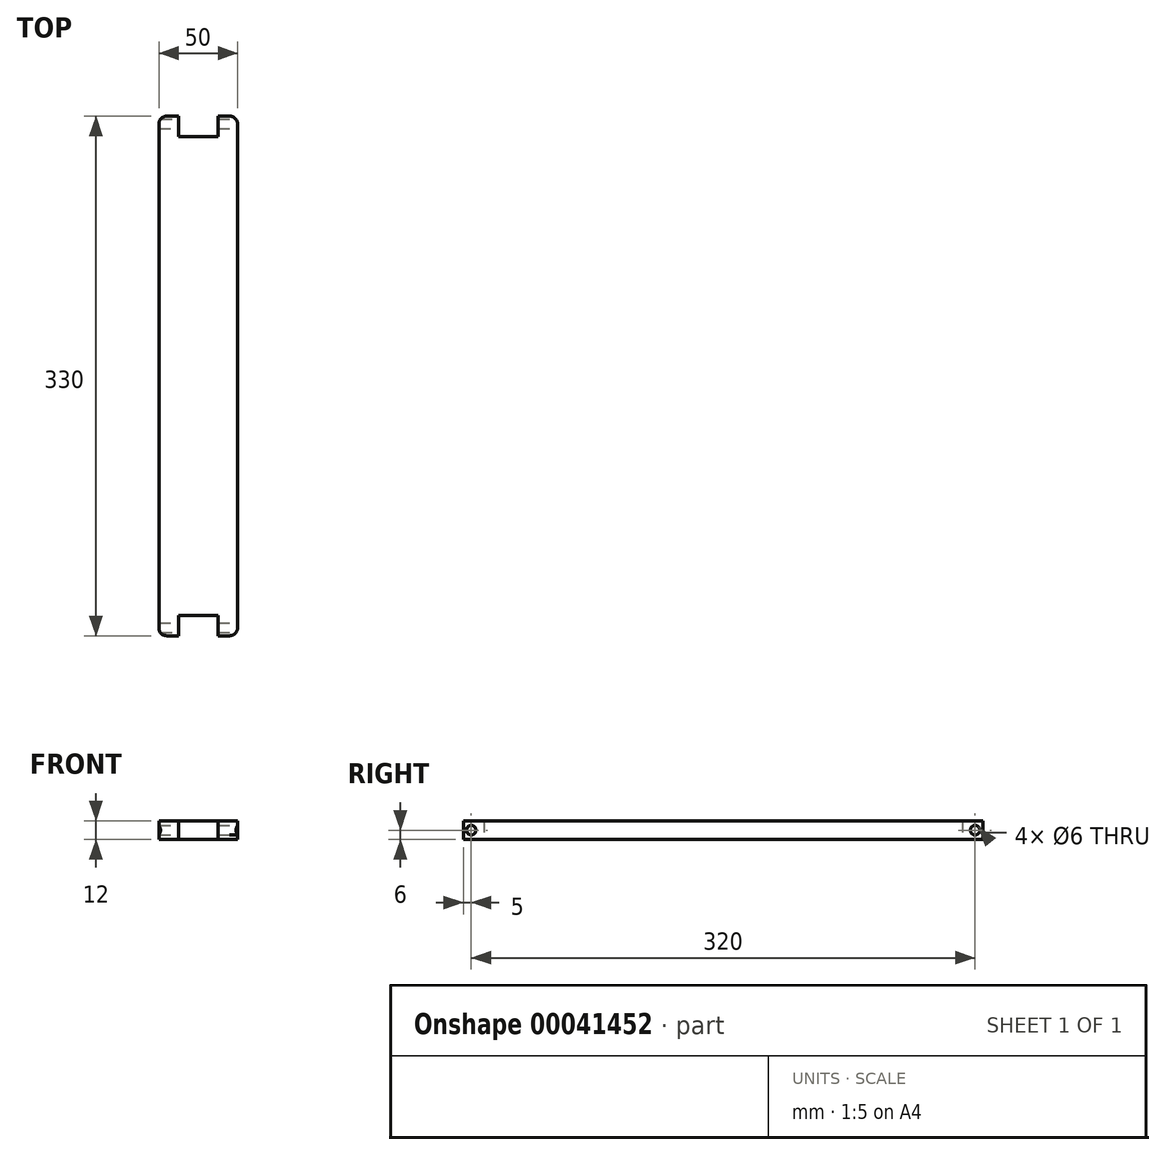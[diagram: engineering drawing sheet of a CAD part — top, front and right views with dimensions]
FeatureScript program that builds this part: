
annotation { "Feature Type Name" : "Feature", "Feature Type Description" : "" }
export const myFeature = defineFeature(function(context is Context, id is Id, definition is map)
    precondition{}
    {
        {
            var Q0;
            Q0=qCreatedBy(makeId("Top.planeOp"),FACE);
            var sketch = newSketch(context, id + "F0", { "sketchPlane" : qUnion([Q0])});
            skLineSegment(sketch, "E0.bottom", {"start": v(-67, 162.6) * mm, "end": v(-54.5, 162.6) * mm});
            skLineSegment(sketch, "E0.top", {"start": v(-67, -167.4) * mm, "end": v(-54.5, -167.4) * mm});
            skLineSegment(sketch, "E0.left", {"start": v(-67, 162.6) * mm, "end": v(-67, -167.4) * mm});
            skLineSegment(sketch, "E0.right", {"start": v(-17, 162.6) * mm, "end": v(-17, -167.4) * mm});
            skLineSegment(sketch, "E1.top", {"start": v(-54.5, 149.6) * mm, "end": v(-29.5, 149.6) * mm});
            skLineSegment(sketch, "E1.left", {"start": v(-54.5, 162.6) * mm, "end": v(-54.5, 149.6) * mm});
            skLineSegment(sketch, "E1.right", {"start": v(-29.5, 162.6) * mm, "end": v(-29.5, 149.6) * mm});
            skLineSegment(sketch, "E2", {"start": v(-54.5, -154.4) * mm, "end": v(-29.5, -154.4) * mm});
            skLineSegment(sketch, "E3.trimOffspring", {"start": v(-54.5, -154.4) * mm, "end": v(-54.5, -167.4) * mm});
            skLineSegment(sketch, "E4.trimOffspring", {"start": v(-29.5, -154.4) * mm, "end": v(-29.5, -167.4) * mm});
            skLineSegment(sketch, "E5.trimOffspring", {"start": v(-29.5, -167.4) * mm, "end": v(-17, -167.4) * mm});
            skLineSegment(sketch, "E6.trimOffspring", {"start": v(-29.5, 162.6) * mm, "end": v(-17, 162.6) * mm});
            skSolve(sketch);
        }
        {
            var Q0;
            Q0 = qSketchRegion(id + "F0", true);
            extrude(context, id + "F1", {"entities" : qUnion([Q0]), "depth" : 12 * mm});
        }
        {
            var Q0;
            Q0=makeQuery(id+"F1.opExtrude","SWEPT_EDGE",EDGE,{"disambiguationData":[OSD([sQuery(id+"F0.wireOp",EDGE,"E0.bottom"),sQuery(id+"F0.wireOp",EDGE,"E0.left")])]});
            fillet(context, id + "F2", {"entities" : qUnion([Q0]), "radius" : 5 * mm, "tangentPropagation" : true, "allowEdgeOverflow" : false});
        }
        {
            var Q0;
            Q0=makeQuery(id+"F1.opExtrude","SWEPT_EDGE",EDGE,{"disambiguationData":[OSD([sQuery(id+"F0.wireOp",EDGE,"E0.top"),sQuery(id+"F0.wireOp",EDGE,"E0.left")])]});
            var Q1;
            Q1=makeQuery(id+"F1.opExtrude","SWEPT_EDGE",EDGE,{"disambiguationData":[OSD([sQuery(id+"F0.wireOp",EDGE,"E0.right"),sQuery(id+"F0.wireOp",EDGE,"E5.trimOffspring")])]});
            var Q2;
            Q2=makeQuery(id+"F1.opExtrude","SWEPT_EDGE",EDGE,{"disambiguationData":[OSD([sQuery(id+"F0.wireOp",EDGE,"E0.right"),sQuery(id+"F0.wireOp",EDGE,"E6.trimOffspring")])]});
            fillet(context, id + "F3", {"entities" : qUnion([Q0, Q1, Q2]), "radius" : 5 * mm, "tangentPropagation" : true, "allowEdgeOverflow" : false});
        }
        {
            var Q0;
            Q0=makeQuery(id+"F1.opExtrude","SWEPT_FACE",FACE,{"disambiguationData":[OSD([sQuery(id+"F0.wireOp",EDGE,"E0.right")])]});
            var sketch = newSketch(context, id + "F4", { "sketchPlane" : qUnion([Q0])});
            skLineSegment(sketch, "E7", {"start": v(-169.22, 6) * mm, "end": v(200.39, 6) * mm, "construction": true});
            skPoint(sketch, "E7.startSnap0", {"position": v(-162.4, 6) * mm});
            skCircle(sketch, "E8", {"center": v(-162.4, 6) * mm, "radius": 3 * mm});
            skCircle(sketch, "E9", {"center": v(157.6, 6) * mm, "radius": 3 * mm});
            skSolve(sketch);
        }
        {
            var Q0;
            {var subQ0=sQuery(id+"F0.wireOp",EDGE,"E0.right");var subQ1=makeQuery(id+"F3.opFillet","BLEND_EDGE",EDGE,{"blendedFrom":[makeQuery(id+"F1.opExtrude","SWEPT_EDGE",EDGE,{"disambiguationData":[OSD([subQ0,sQuery(id+"F0.wireOp",EDGE,"E6.trimOffspring")])]}),makeQuery(id+"F1.opExtrude","SWEPT_FACE",FACE,{"disambiguationData":[OSD([subQ0])]})],"blendedInto":[makeQuery(id+"F1.opExtrude","SWEPT_FACE",FACE,{"disambiguationData":[OSD([subQ0])]})]});var subQ2=sQuery(id+"F4.wireOp",EDGE,"E9");var subQ4=makeQuery(id+"F4.imprint","INTERSECT",VERTEX,{"disambiguationData":[OD(0.0)],"derivedFrom":[subQ1,subQ2]});Q0=makeQuery(id+"F4.imprint","IMPRINT",FACE,{"disambiguationData":[TD([[makeQuery(id+"F4.imprint","IMPRINT",EDGE,{"disambiguationData":[TD([[subQ4,1.0]])],"derivedFrom":subQ2}),1.0]])]});}
            var Q1;
            {var subQ0=sQuery(id+"F0.wireOp",EDGE,"E0.right");var subQ1=makeQuery(id+"F3.opFillet","BLEND_EDGE",EDGE,{"blendedFrom":[makeQuery(id+"F1.opExtrude","SWEPT_EDGE",EDGE,{"disambiguationData":[OSD([subQ0,sQuery(id+"F0.wireOp",EDGE,"E6.trimOffspring")])]}),makeQuery(id+"F1.opExtrude","SWEPT_FACE",FACE,{"disambiguationData":[OSD([subQ0])]})],"blendedInto":[makeQuery(id+"F1.opExtrude","SWEPT_FACE",FACE,{"disambiguationData":[OSD([subQ0])]})]});var subQ2=sQuery(id+"F4.wireOp",EDGE,"E9");var subQ4=makeQuery(id+"F4.imprint","INTERSECT",VERTEX,{"disambiguationData":[OD(0.0)],"derivedFrom":[subQ1,subQ2]});Q1=makeQuery(id+"F4.imprint","IMPRINT",FACE,{"disambiguationData":[TD([[makeQuery(id+"F4.imprint","IMPRINT",EDGE,{"disambiguationData":[TD([[subQ4,-1.0]])],"derivedFrom":subQ2}),1.0]])]});}
            var Q2;
            {var subQ0=sQuery(id+"F0.wireOp",EDGE,"E0.right");var subQ1=makeQuery(id+"F3.opFillet","BLEND_EDGE",EDGE,{"blendedFrom":[makeQuery(id+"F1.opExtrude","SWEPT_EDGE",EDGE,{"disambiguationData":[OSD([subQ0,sQuery(id+"F0.wireOp",EDGE,"E5.trimOffspring")])]}),makeQuery(id+"F1.opExtrude","SWEPT_FACE",FACE,{"disambiguationData":[OSD([subQ0])]})],"blendedInto":[makeQuery(id+"F1.opExtrude","SWEPT_FACE",FACE,{"disambiguationData":[OSD([subQ0])]})]});var subQ2=sQuery(id+"F4.wireOp",EDGE,"E8");var subQ4=makeQuery(id+"F4.imprint","INTERSECT",VERTEX,{"disambiguationData":[OD(0.0)],"derivedFrom":[subQ1,subQ2]});Q2=makeQuery(id+"F4.imprint","IMPRINT",FACE,{"disambiguationData":[TD([[makeQuery(id+"F4.imprint","IMPRINT",EDGE,{"disambiguationData":[TD([[subQ4,-1.0]])],"derivedFrom":subQ2}),1.0]])]});}
            var Q3;
            {var subQ0=sQuery(id+"F0.wireOp",EDGE,"E0.right");var subQ1=makeQuery(id+"F3.opFillet","BLEND_EDGE",EDGE,{"blendedFrom":[makeQuery(id+"F1.opExtrude","SWEPT_EDGE",EDGE,{"disambiguationData":[OSD([subQ0,sQuery(id+"F0.wireOp",EDGE,"E5.trimOffspring")])]}),makeQuery(id+"F1.opExtrude","SWEPT_FACE",FACE,{"disambiguationData":[OSD([subQ0])]})],"blendedInto":[makeQuery(id+"F1.opExtrude","SWEPT_FACE",FACE,{"disambiguationData":[OSD([subQ0])]})]});var subQ2=sQuery(id+"F4.wireOp",EDGE,"E8");var subQ4=makeQuery(id+"F4.imprint","INTERSECT",VERTEX,{"disambiguationData":[OD(0.0)],"derivedFrom":[subQ1,subQ2]});Q3=makeQuery(id+"F4.imprint","IMPRINT",FACE,{"disambiguationData":[TD([[makeQuery(id+"F4.imprint","IMPRINT",EDGE,{"disambiguationData":[TD([[subQ4,1.0]])],"derivedFrom":subQ2}),1.0]])]});}
            var Q4;
            Q4=sQuery(id+"F4.wireOp",EDGE,"E9");
            extrude(context, id + "F5", {"entities" : qUnion([Q0, Q1, Q2, Q3]), "operationType" : NewBodyOperationType.REMOVE, "surfaceEntities" : qUnion([Q4]), "endBound" : BoundingType.THROUGH_ALL, "oppositeDirection" : true, "depth" : 25 * mm});
        }
    });
